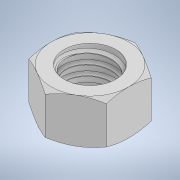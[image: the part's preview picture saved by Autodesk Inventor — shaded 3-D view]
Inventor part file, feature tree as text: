
AUTODESK INVENTOR PART (.ipt)
format: ipt  version: 2021 (Build 250183000, 183)  size: 273,408 bytes
history: native  units: in
note: dims shown in document units (in); Inventor stores cm internally (conversion verified against a paired STEP export)
features: mirror x1
ambient origin geometry x8: Origin, YZ Plane, XZ Plane, XY Plane, X Axis, Y Axis, Z Axis, Center Point
bodies: Solid1 (feature_tree)
feature tree (1):
  mirror  "Mirror1"
